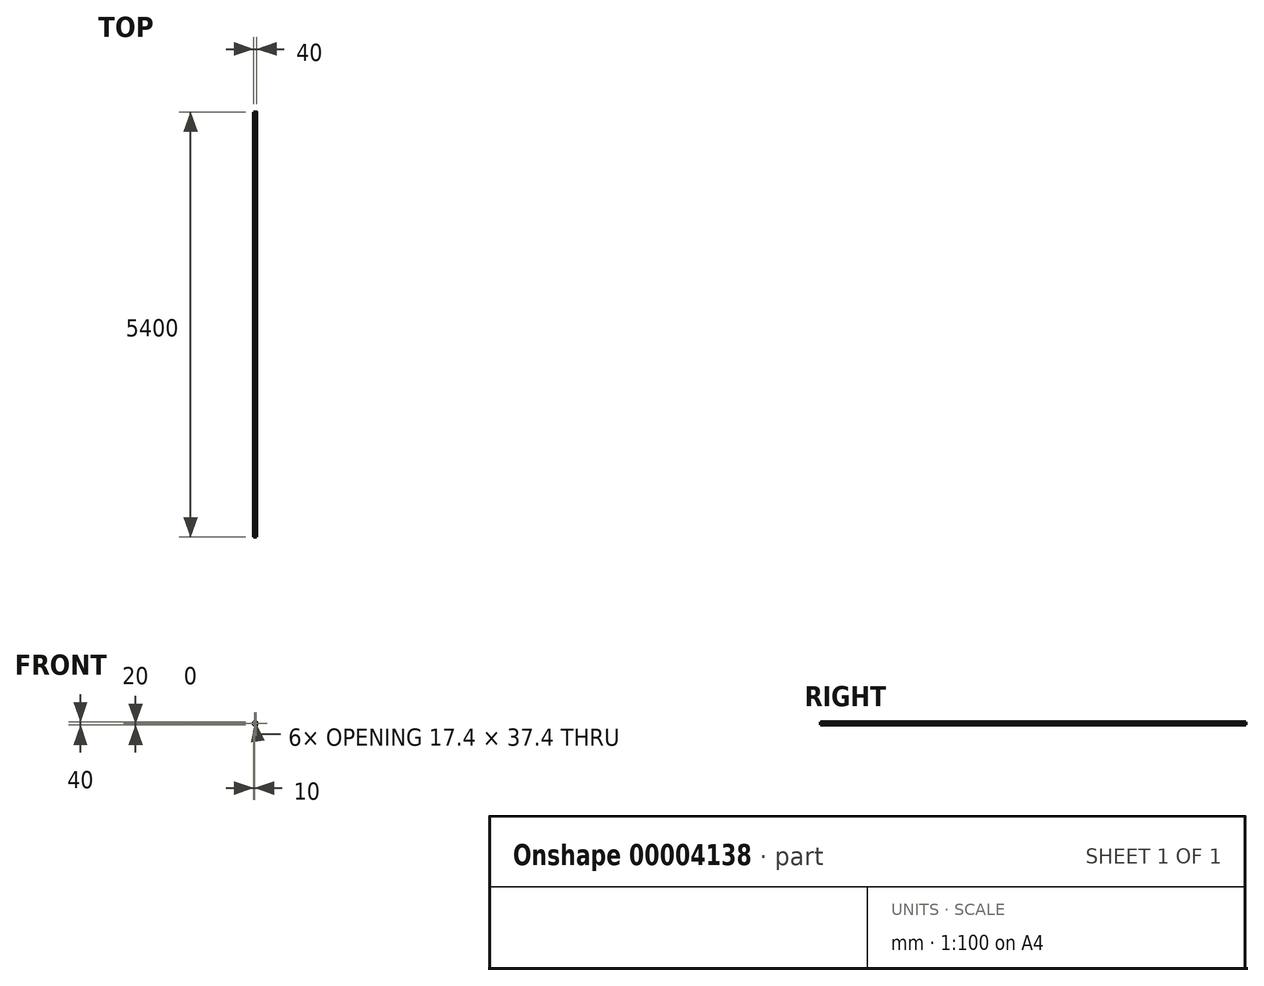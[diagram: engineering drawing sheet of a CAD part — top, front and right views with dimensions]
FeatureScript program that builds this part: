
annotation { "Feature Type Name" : "Feature", "Feature Type Description" : "" }
export const myFeature = defineFeature(function(context is Context, id is Id, definition is map)
    precondition{}
    {
        {
            var Q0;
            Q0=qCreatedBy(makeId("Front.planeOp"),FACE);
            var sketch = newSketch(context, id + "F0", { "sketchPlane" : qUnion([Q0])});
            skLineSegment(sketch, "E0.rect.bottom", {"start": v(20, -20) * mm, "end": v(-20, -20) * mm, "construction": true});
            skLineSegment(sketch, "E0.rect.top", {"start": v(20, 20) * mm, "end": v(-20, 20) * mm, "construction": true});
            skLineSegment(sketch, "E0.rect.left", {"start": v(20, -20) * mm, "end": v(20, 20) * mm, "construction": true});
            skLineSegment(sketch, "E0.rect.right", {"start": v(-20, -20) * mm, "end": v(-20, 20) * mm, "construction": true});
            skPoint(sketch, "E0.rect.middle", {"position": v(0, 0) * mm});
            skLineSegment(sketch, "E1", {"start": v(0, 20) * mm, "end": v(0, -20) * mm, "construction": true});
            skLineSegment(sketch, "E2", {"start": v(20, -20) * mm, "end": v(20, -5.5) * mm});
            skLineSegment(sketch, "E3", {"start": v(20, 5.5) * mm, "end": v(20, 20) * mm});
            skLineSegment(sketch, "E4", {"start": v(20, 20) * mm, "end": v(4.2, 20) * mm});
            skLineSegment(sketch, "E5", {"start": v(20, -20) * mm, "end": v(5.2, -20) * mm});
            skArc(sketch, "E6", {"start": v(20, 5.5) * mm, "mid": v(18.29, 0) * mm, "end": v(20, -5.5) * mm});
            skLineSegment(sketch, "E7", {"start": v(5.2, -20) * mm, "end": v(5.2, -17) * mm});
            skLineSegment(sketch, "E8", {"start": v(5.2, -17) * mm, "end": v(8.6, -17) * mm});
            skLineSegment(sketch, "E9", {"start": v(8.6, -17) * mm, "end": v(8.6, -9.1) * mm});
            skLineSegment(sketch, "E10", {"start": v(0, -9.1) * mm, "end": v(0, 2.5) * mm});
            skLineSegment(sketch, "E11", {"start": v(6.7, 17) * mm, "end": v(6.7, 14) * mm});
            skArc(sketch, "E12", {"start": v(6.7, 9) * mm, "mid": v(7.58, 11.5) * mm, "end": v(6.7, 14) * mm});
            skLineSegment(sketch, "E13", {"start": v(4, 6) * mm, "end": v(6.7, 6) * mm});
            skLineSegment(sketch, "E14", {"start": v(6.7, 6) * mm, "end": v(6.7, 9) * mm});
            skLineSegment(sketch, "E15", {"start": v(4, 6) * mm, "end": v(4, 2.5) * mm});
            skLineSegment(sketch, "E16", {"start": v(4, 2.5) * mm, "end": v(0, 2.5) * mm});
            skLineSegment(sketch, "E17", {"start": v(8.6, -9.1) * mm, "end": v(0, -9.1) * mm});
            skLineSegment(sketch, "E18", {"start": v(4.2, 20) * mm, "end": v(4.2, 17) * mm});
            skLineSegment(sketch, "E19", {"start": v(4.2, 17) * mm, "end": v(6.7, 17) * mm});
            skLineSegment(sketch, "E20.0", {"start": v(18.7, 5.9) * mm, "end": v(18.7, 18.7) * mm});
            skArc(sketch, "E20.1", {"start": v(18.7, 5.9) * mm, "mid": v(16.99, 0) * mm, "end": v(18.7, -5.9) * mm});
            skLineSegment(sketch, "E20.2", {"start": v(18.7, -18.7) * mm, "end": v(18.7, -5.9) * mm});
            skLineSegment(sketch, "E20.3", {"start": v(18.7, -18.7) * mm, "end": v(9.9, -18.7) * mm});
            skLineSegment(sketch, "E20.4", {"start": v(9.9, -18.7) * mm, "end": v(9.9, -7.8) * mm});
            skLineSegment(sketch, "E20.5", {"start": v(18.7, 18.7) * mm, "end": v(8, 18.7) * mm});
            skLineSegment(sketch, "E20.6", {"start": v(9.9, -7.8) * mm, "end": v(1.3, -7.8) * mm});
            skLineSegment(sketch, "E20.7", {"start": v(1.3, -7.8) * mm, "end": v(1.3, 1.2) * mm});
            skLineSegment(sketch, "E20.8", {"start": v(5.3, 1.2) * mm, "end": v(1.3, 1.2) * mm});
            skLineSegment(sketch, "E20.9", {"start": v(5.3, 4.7) * mm, "end": v(5.3, 1.2) * mm});
            skLineSegment(sketch, "E20.10", {"start": v(5.3, 4.7) * mm, "end": v(8, 4.7) * mm});
            skLineSegment(sketch, "E20.11", {"start": v(8, 4.7) * mm, "end": v(8, 8.58) * mm});
            skArc(sketch, "E20.12", {"start": v(8, 8.58) * mm, "mid": v(8.88, 11.5) * mm, "end": v(8, 14.42) * mm});
            skLineSegment(sketch, "E20.13", {"start": v(8, 18.7) * mm, "end": v(8, 14.42) * mm});
            skLineSegment(sketch, "E21.0.MirrorCS", {"start": v(-4.2, 20) * mm, "end": v(-4.2, 17) * mm});
            skLineSegment(sketch, "E21.1.MirrorCS", {"start": v(-4.2, 17) * mm, "end": v(-6.7, 17) * mm});
            skLineSegment(sketch, "E21.2.MirrorCS", {"start": v(-6.7, 17) * mm, "end": v(-6.7, 14) * mm});
            skLineSegment(sketch, "E21.3.MirrorCS", {"start": v(-8, 18.7) * mm, "end": v(-8, 14.42) * mm});
            skArc(sketch, "E21.4.MirrorCS", {"start": v(-8, 8.58) * mm, "mid": v(-8.88, 11.5) * mm, "end": v(-8, 14.42) * mm});
            skArc(sketch, "E21.5.MirrorCS", {"start": v(-6.7, 9) * mm, "mid": v(-7.58, 11.5) * mm, "end": v(-6.7, 14) * mm});
            skLineSegment(sketch, "E21.6.MirrorCS", {"start": v(-6.7, 6) * mm, "end": v(-6.7, 9) * mm});
            skLineSegment(sketch, "E21.7.MirrorCS", {"start": v(-8, 4.7) * mm, "end": v(-8, 8.58) * mm});
            skLineSegment(sketch, "E21.8.MirrorCS", {"start": v(-5.3, 4.7) * mm, "end": v(-8, 4.7) * mm});
            skLineSegment(sketch, "E21.9.MirrorCS", {"start": v(-4, 6) * mm, "end": v(-6.7, 6) * mm});
            skLineSegment(sketch, "E21.10.MirrorCS", {"start": v(-4, 6) * mm, "end": v(-4, 2.5) * mm});
            skLineSegment(sketch, "E21.11.MirrorCS", {"start": v(-5.3, 4.7) * mm, "end": v(-5.3, 1.2) * mm});
            skLineSegment(sketch, "E21.12.MirrorCS", {"start": v(-5.3, 1.2) * mm, "end": v(-1.3, 1.2) * mm});
            skLineSegment(sketch, "E21.13.MirrorCS", {"start": v(-4, 2.5) * mm, "end": v(0, 2.5) * mm});
            skLineSegment(sketch, "E21.14.MirrorCS", {"start": v(-1.3, -7.8) * mm, "end": v(-1.3, 1.2) * mm});
            skLineSegment(sketch, "E21.15.MirrorCS", {"start": v(-8.6, -9.1) * mm, "end": v(0, -9.1) * mm});
            skLineSegment(sketch, "E21.16.MirrorCS", {"start": v(-9.9, -7.8) * mm, "end": v(-1.3, -7.8) * mm});
            skLineSegment(sketch, "E21.17.MirrorCS", {"start": v(-9.9, -18.7) * mm, "end": v(-9.9, -7.8) * mm});
            skLineSegment(sketch, "E21.18.MirrorCS", {"start": v(-8.6, -17) * mm, "end": v(-8.6, -9.1) * mm});
            skLineSegment(sketch, "E21.19.MirrorCS", {"start": v(-5.2, -17) * mm, "end": v(-8.6, -17) * mm});
            skLineSegment(sketch, "E21.20.MirrorCS", {"start": v(-5.2, -20) * mm, "end": v(-5.2, -17) * mm});
            skLineSegment(sketch, "E21.21.MirrorCS", {"start": v(-18.7, -18.7) * mm, "end": v(-9.9, -18.7) * mm});
            skLineSegment(sketch, "E21.22.MirrorCS", {"start": v(-20, -20) * mm, "end": v(-5.2, -20) * mm});
            skLineSegment(sketch, "E21.23.MirrorCS", {"start": v(-18.7, -18.7) * mm, "end": v(-18.7, -5.9) * mm});
            skLineSegment(sketch, "E21.24.MirrorCS", {"start": v(-20, -20) * mm, "end": v(-20, -5.5) * mm});
            skArc(sketch, "E21.25.MirrorCS", {"start": v(-18.7, 5.9) * mm, "mid": v(-16.99, 0) * mm, "end": v(-18.7, -5.9) * mm});
            skArc(sketch, "E21.26.MirrorCS", {"start": v(-20, 5.5) * mm, "mid": v(-18.29, 0) * mm, "end": v(-20, -5.5) * mm});
            skLineSegment(sketch, "E21.27.MirrorCS", {"start": v(-18.7, 5.9) * mm, "end": v(-18.7, 18.7) * mm});
            skLineSegment(sketch, "E21.28.MirrorCS", {"start": v(-20, 5.5) * mm, "end": v(-20, 20) * mm});
            skLineSegment(sketch, "E21.29.MirrorCS", {"start": v(-20, 20) * mm, "end": v(-4.2, 20) * mm});
            skLineSegment(sketch, "E21.30.MirrorCS", {"start": v(-18.7, 18.7) * mm, "end": v(-8, 18.7) * mm});
            skSolve(sketch);
        }
        {
            var Q0;
            Q0=makeQuery(id+"F0.imprint","IMPRINT",FACE,{"disambiguationData":[TD([[makeQuery(id+"F0.imprint","IMPRINT",EDGE,{"derivedFrom":sQuery(id+"F0.wireOp",EDGE,"E2")}),1.0]])]});
            var Q1;
            Q1=makeQuery(id+"F0.imprint","IMPRINT",FACE,{"disambiguationData":[TD([[makeQuery(id+"F0.imprint","IMPRINT",EDGE,{"derivedFrom":sQuery(id+"F0.wireOp",EDGE,"E10")}),1.0]])]});
            extrude(context, id + "F1", {"entities" : qUnion([Q0, Q1]), "oppositeDirection" : true, "depth" : 50 * mm});
        }
        {
            var Q0;
            Q0=makeQuery(id+"F0.imprint","IMPRINT",FACE,{"disambiguationData":[TD([[makeQuery(id+"F0.imprint","IMPRINT",EDGE,{"derivedFrom":sQuery(id+"F0.wireOp",EDGE,"E10")}),1.0]])]});
            var Q1;
            Q1=makeQuery(id+"F0.imprint","IMPRINT",FACE,{"disambiguationData":[TD([[makeQuery(id+"F0.imprint","IMPRINT",EDGE,{"derivedFrom":sQuery(id+"F0.wireOp",EDGE,"E2")}),1.0]])]});
            extrude(context, id + "F2", {"entities" : qUnion([Q0, Q1]), "oppositeDirection" : true, "depth" : 3500 * mm});
        }
        {
            var Q0;
            Q0=makeQuery(id+"F0.imprint","IMPRINT",FACE,{"disambiguationData":[TD([[makeQuery(id+"F0.imprint","IMPRINT",EDGE,{"derivedFrom":sQuery(id+"F0.wireOp",EDGE,"E10")}),1.0]])]});
            var Q1;
            Q1=makeQuery(id+"F0.imprint","IMPRINT",FACE,{"disambiguationData":[TD([[makeQuery(id+"F0.imprint","IMPRINT",EDGE,{"derivedFrom":sQuery(id+"F0.wireOp",EDGE,"E2")}),1.0]])]});
            extrude(context, id + "F3", {"entities" : qUnion([Q0, Q1]), "oppositeDirection" : true, "depth" : (3 * 1800) * mm});
        }
        {
            var Q0;
            Q0=makeQuery(id+"F1.opExtrude","SWEPT_EDGE",EDGE,{"disambiguationData":[OSD([sQuery(id+"F0.wireOp",EDGE,"E21.28.MirrorCS"),sQuery(id+"F0.wireOp",EDGE,"E21.29.MirrorCS")])]});
            var Q1;
            Q1=makeQuery(id+"F1.opExtrude","SWEPT_EDGE",EDGE,{"disambiguationData":[OSD([sQuery(id+"F0.wireOp",EDGE,"E21.0.MirrorCS"),sQuery(id+"F0.wireOp",EDGE,"E21.29.MirrorCS")])]});
            var Q2;
            Q2=makeQuery(id+"F1.opExtrude","SWEPT_EDGE",EDGE,{"disambiguationData":[OSD([sQuery(id+"F0.wireOp",EDGE,"E4"),sQuery(id+"F0.wireOp",EDGE,"E18")])]});
            var Q3;
            Q3=makeQuery(id+"F1.opExtrude","SWEPT_EDGE",EDGE,{"disambiguationData":[OSD([sQuery(id+"F0.wireOp",EDGE,"E3"),sQuery(id+"F0.wireOp",EDGE,"E4")])]});
            var Q4;
            Q4=makeQuery(id+"F1.opExtrude","SWEPT_EDGE",EDGE,{"disambiguationData":[OSD([sQuery(id+"F0.wireOp",EDGE,"E21.22.MirrorCS"),sQuery(id+"F0.wireOp",EDGE,"E21.24.MirrorCS")])]});
            var Q5;
            Q5=makeQuery(id+"F1.opExtrude","SWEPT_EDGE",EDGE,{"disambiguationData":[OSD([sQuery(id+"F0.wireOp",EDGE,"E2"),sQuery(id+"F0.wireOp",EDGE,"E5")])]});
            var Q6;
            Q6=makeQuery(id+"F1.opExtrude","SWEPT_EDGE",EDGE,{"disambiguationData":[OSD([sQuery(id+"F0.wireOp",EDGE,"E20.4"),sQuery(id+"F0.wireOp",EDGE,"E20.6")])]});
            var Q7;
            Q7=makeQuery(id+"F1.opExtrude","SWEPT_EDGE",EDGE,{"disambiguationData":[OSD([sQuery(id+"F0.wireOp",EDGE,"E21.16.MirrorCS"),sQuery(id+"F0.wireOp",EDGE,"E21.17.MirrorCS")])]});
            var Q8;
            Q8=makeQuery(id+"F1.opExtrude","SWEPT_EDGE",EDGE,{"disambiguationData":[OSD([sQuery(id+"F0.wireOp",EDGE,"E20.4"),sQuery(id+"F0.wireOp",EDGE,"E20.6")])]});
            var Q9;
            Q9=makeQuery(id+"F1.opExtrude","SWEPT_EDGE",EDGE,{"disambiguationData":[OSD([sQuery(id+"F0.wireOp",EDGE,"E21.16.MirrorCS"),sQuery(id+"F0.wireOp",EDGE,"E21.17.MirrorCS")])]});
            fillet(context, id + "F4", {"entities" : qUnion([Q0, Q1, Q2, Q3, Q4, Q5, Q6, Q7, Q8, Q9]), "radius" : 0.8 * mm, "tangentPropagation" : true, "allowEdgeOverflow" : false});
        }
        {
            var Q0;
            Q0=makeQuery(id+"F1.opExtrude","SWEPT_EDGE",EDGE,{"disambiguationData":[OSD([sQuery(id+"F0.wireOp",EDGE,"E15"),sQuery(id+"F0.wireOp",EDGE,"E16")])]});
            var Q1;
            Q1=makeQuery(id+"F1.opExtrude","SWEPT_EDGE",EDGE,{"disambiguationData":[OSD([sQuery(id+"F0.wireOp",EDGE,"E13"),sQuery(id+"F0.wireOp",EDGE,"E15")])]});
            var Q2;
            Q2=makeQuery(id+"F1.opExtrude","SWEPT_EDGE",EDGE,{"disambiguationData":[OSD([sQuery(id+"F0.wireOp",EDGE,"E13"),sQuery(id+"F0.wireOp",EDGE,"E14")])]});
            var Q3;
            Q3=makeQuery(id+"F1.opExtrude","SWEPT_EDGE",EDGE,{"disambiguationData":[OSD([sQuery(id+"F0.wireOp",EDGE,"E12"),sQuery(id+"F0.wireOp",EDGE,"E14")])]});
            var Q4;
            Q4=makeQuery(id+"F1.opExtrude","SWEPT_EDGE",EDGE,{"disambiguationData":[OSD([sQuery(id+"F0.wireOp",EDGE,"E11"),sQuery(id+"F0.wireOp",EDGE,"E12")])]});
            var Q5;
            Q5=makeQuery(id+"F1.opExtrude","SWEPT_EDGE",EDGE,{"disambiguationData":[OSD([sQuery(id+"F0.wireOp",EDGE,"E21.2.MirrorCS"),sQuery(id+"F0.wireOp",EDGE,"E21.5.MirrorCS")])]});
            var Q6;
            Q6=makeQuery(id+"F1.opExtrude","SWEPT_EDGE",EDGE,{"disambiguationData":[OSD([sQuery(id+"F0.wireOp",EDGE,"E21.5.MirrorCS"),sQuery(id+"F0.wireOp",EDGE,"E21.6.MirrorCS")])]});
            var Q7;
            Q7=makeQuery(id+"F1.opExtrude","SWEPT_EDGE",EDGE,{"disambiguationData":[OSD([sQuery(id+"F0.wireOp",EDGE,"E21.9.MirrorCS"),sQuery(id+"F0.wireOp",EDGE,"E21.10.MirrorCS")])]});
            var Q8;
            Q8=makeQuery(id+"F1.opExtrude","SWEPT_EDGE",EDGE,{"disambiguationData":[OSD([sQuery(id+"F0.wireOp",EDGE,"E21.10.MirrorCS"),sQuery(id+"F0.wireOp",EDGE,"E21.13.MirrorCS")])]});
            fillet(context, id + "F5", {"entities" : qUnion([Q0, Q1, Q2, Q3, Q4, Q5, Q6, Q7, Q8]), "radius" : 0.8 * mm, "tangentPropagation" : true, "allowEdgeOverflow" : false});
        }
        {
            var Q0;
            Q0=makeQuery(id+"F1.opExtrude","SWEPT_EDGE",EDGE,{"disambiguationData":[OSD([sQuery(id+"F0.wireOp",EDGE,"E20.6"),sQuery(id+"F0.wireOp",EDGE,"E20.7")])]});
            var Q1;
            Q1=makeQuery(id+"F1.opExtrude","SWEPT_EDGE",EDGE,{"disambiguationData":[OSD([sQuery(id+"F0.wireOp",EDGE,"E20.7"),sQuery(id+"F0.wireOp",EDGE,"E20.8")])]});
            var Q2;
            Q2=makeQuery(id+"F1.opExtrude","SWEPT_EDGE",EDGE,{"disambiguationData":[OSD([sQuery(id+"F0.wireOp",EDGE,"E20.8"),sQuery(id+"F0.wireOp",EDGE,"E20.9")])]});
            var Q3;
            Q3=makeQuery(id+"F1.opExtrude","SWEPT_EDGE",EDGE,{"disambiguationData":[OSD([sQuery(id+"F0.wireOp",EDGE,"E20.9"),sQuery(id+"F0.wireOp",EDGE,"E20.10")])]});
            var Q4;
            Q4=makeQuery(id+"F1.opExtrude","SWEPT_EDGE",EDGE,{"disambiguationData":[OSD([sQuery(id+"F0.wireOp",EDGE,"E20.10"),sQuery(id+"F0.wireOp",EDGE,"E20.11")])]});
            var Q5;
            Q5=makeQuery(id+"F1.opExtrude","SWEPT_EDGE",EDGE,{"disambiguationData":[OSD([sQuery(id+"F0.wireOp",EDGE,"E21.14.MirrorCS"),sQuery(id+"F0.wireOp",EDGE,"E21.16.MirrorCS")])]});
            var Q6;
            Q6=makeQuery(id+"F1.opExtrude","SWEPT_EDGE",EDGE,{"disambiguationData":[OSD([sQuery(id+"F0.wireOp",EDGE,"E21.12.MirrorCS"),sQuery(id+"F0.wireOp",EDGE,"E21.14.MirrorCS")])]});
            var Q7;
            Q7=makeQuery(id+"F1.opExtrude","SWEPT_EDGE",EDGE,{"disambiguationData":[OSD([sQuery(id+"F0.wireOp",EDGE,"E21.11.MirrorCS"),sQuery(id+"F0.wireOp",EDGE,"E21.12.MirrorCS")])]});
            var Q8;
            Q8=makeQuery(id+"F1.opExtrude","SWEPT_EDGE",EDGE,{"disambiguationData":[OSD([sQuery(id+"F0.wireOp",EDGE,"E21.8.MirrorCS"),sQuery(id+"F0.wireOp",EDGE,"E21.11.MirrorCS")])]});
            var Q9;
            Q9=makeQuery(id+"F1.opExtrude","SWEPT_EDGE",EDGE,{"disambiguationData":[OSD([sQuery(id+"F0.wireOp",EDGE,"E21.7.MirrorCS"),sQuery(id+"F0.wireOp",EDGE,"E21.8.MirrorCS")])]});
            fillet(context, id + "F6", {"entities" : qUnion([Q0, Q1, Q2, Q3, Q4, Q5, Q6, Q7, Q8, Q9]), "radius" : .4 * mm, "tangentPropagation" : true, "allowEdgeOverflow" : false});
        }
        {
            var Q0;
            Q0=makeQuery(id+"F3.opExtrude","SWEPT_EDGE",EDGE,{"disambiguationData":[OSD([sQuery(id+"F0.wireOp",EDGE,"E21.28.MirrorCS"),sQuery(id+"F0.wireOp",EDGE,"E21.29.MirrorCS")])]});
            var Q1;
            Q1=makeQuery(id+"F3.opExtrude","SWEPT_EDGE",EDGE,{"disambiguationData":[OSD([sQuery(id+"F0.wireOp",EDGE,"E3"),sQuery(id+"F0.wireOp",EDGE,"E4")])]});
            var Q2;
            Q2=makeQuery(id+"F3.opExtrude","SWEPT_EDGE",EDGE,{"disambiguationData":[OSD([sQuery(id+"F0.wireOp",EDGE,"E2"),sQuery(id+"F0.wireOp",EDGE,"E5")])]});
            var Q3;
            Q3=makeQuery(id+"F3.opExtrude","SWEPT_EDGE",EDGE,{"disambiguationData":[OSD([sQuery(id+"F0.wireOp",EDGE,"E20.4"),sQuery(id+"F0.wireOp",EDGE,"E20.6")])]});
            var Q4;
            Q4=makeQuery(id+"F3.opExtrude","SWEPT_EDGE",EDGE,{"disambiguationData":[OSD([sQuery(id+"F0.wireOp",EDGE,"E21.16.MirrorCS"),sQuery(id+"F0.wireOp",EDGE,"E21.17.MirrorCS")])]});
            var Q5;
            Q5=makeQuery(id+"F3.opExtrude","SWEPT_EDGE",EDGE,{"disambiguationData":[OSD([sQuery(id+"F0.wireOp",EDGE,"E21.22.MirrorCS"),sQuery(id+"F0.wireOp",EDGE,"E21.24.MirrorCS")])]});
            fillet(context, id + "F7", {"entities" : qUnion([Q0, Q1, Q2, Q3, Q4, Q5]), "radius" : 0.8 * mm, "tangentPropagation" : true, "allowEdgeOverflow" : false});
        }
        {
            var Q0;
            Q0=makeQuery(id+"F3.opExtrude","SWEPT_EDGE",EDGE,{"disambiguationData":[OSD([sQuery(id+"F0.wireOp",EDGE,"E21.2.MirrorCS"),sQuery(id+"F0.wireOp",EDGE,"E21.5.MirrorCS")])]});
            var Q1;
            Q1=makeQuery(id+"F3.opExtrude","SWEPT_EDGE",EDGE,{"disambiguationData":[OSD([sQuery(id+"F0.wireOp",EDGE,"E21.5.MirrorCS"),sQuery(id+"F0.wireOp",EDGE,"E21.6.MirrorCS")])]});
            var Q2;
            Q2=makeQuery(id+"F3.opExtrude","SWEPT_EDGE",EDGE,{"disambiguationData":[OSD([sQuery(id+"F0.wireOp",EDGE,"E21.6.MirrorCS"),sQuery(id+"F0.wireOp",EDGE,"E21.9.MirrorCS")])]});
            var Q3;
            Q3=makeQuery(id+"F3.opExtrude","SWEPT_EDGE",EDGE,{"disambiguationData":[OSD([sQuery(id+"F0.wireOp",EDGE,"E21.9.MirrorCS"),sQuery(id+"F0.wireOp",EDGE,"E21.10.MirrorCS")])]});
            var Q4;
            Q4=makeQuery(id+"F3.opExtrude","SWEPT_EDGE",EDGE,{"disambiguationData":[OSD([sQuery(id+"F0.wireOp",EDGE,"E21.10.MirrorCS"),sQuery(id+"F0.wireOp",EDGE,"E21.13.MirrorCS")])]});
            var Q5;
            Q5=makeQuery(id+"F3.opExtrude","SWEPT_EDGE",EDGE,{"disambiguationData":[OSD([sQuery(id+"F0.wireOp",EDGE,"E15"),sQuery(id+"F0.wireOp",EDGE,"E16")])]});
            var Q6;
            Q6=makeQuery(id+"F3.opExtrude","SWEPT_EDGE",EDGE,{"disambiguationData":[OSD([sQuery(id+"F0.wireOp",EDGE,"E13"),sQuery(id+"F0.wireOp",EDGE,"E15")])]});
            var Q7;
            Q7=makeQuery(id+"F3.opExtrude","SWEPT_EDGE",EDGE,{"disambiguationData":[OSD([sQuery(id+"F0.wireOp",EDGE,"E13"),sQuery(id+"F0.wireOp",EDGE,"E14")])]});
            var Q8;
            Q8=makeQuery(id+"F3.opExtrude","SWEPT_EDGE",EDGE,{"disambiguationData":[OSD([sQuery(id+"F0.wireOp",EDGE,"E12"),sQuery(id+"F0.wireOp",EDGE,"E14")])]});
            var Q9;
            Q9=makeQuery(id+"F3.opExtrude","SWEPT_EDGE",EDGE,{"disambiguationData":[OSD([sQuery(id+"F0.wireOp",EDGE,"E11"),sQuery(id+"F0.wireOp",EDGE,"E12")])]});
            fillet(context, id + "F8", {"entities" : qUnion([Q0, Q1, Q2, Q3, Q4, Q5, Q6, Q7, Q8, Q9]), "radius" : 0.6 * mm, "tangentPropagation" : true, "allowEdgeOverflow" : false});
        }
        {
            var Q0;
            Q0=makeQuery(id+"F3.opExtrude","SWEPT_EDGE",EDGE,{"disambiguationData":[OSD([sQuery(id+"F0.wireOp",EDGE,"E20.10"),sQuery(id+"F0.wireOp",EDGE,"E20.11")])]});
            var Q1;
            Q1=makeQuery(id+"F3.opExtrude","SWEPT_EDGE",EDGE,{"disambiguationData":[OSD([sQuery(id+"F0.wireOp",EDGE,"E20.8"),sQuery(id+"F0.wireOp",EDGE,"E20.9")])]});
            var Q2;
            Q2=makeQuery(id+"F3.opExtrude","SWEPT_EDGE",EDGE,{"disambiguationData":[OSD([sQuery(id+"F0.wireOp",EDGE,"E20.9"),sQuery(id+"F0.wireOp",EDGE,"E20.10")])]});
            var Q3;
            Q3=makeQuery(id+"F3.opExtrude","SWEPT_EDGE",EDGE,{"disambiguationData":[OSD([sQuery(id+"F0.wireOp",EDGE,"E20.7"),sQuery(id+"F0.wireOp",EDGE,"E20.8")])]});
            var Q4;
            Q4=makeQuery(id+"F3.opExtrude","SWEPT_EDGE",EDGE,{"disambiguationData":[OSD([sQuery(id+"F0.wireOp",EDGE,"E20.6"),sQuery(id+"F0.wireOp",EDGE,"E20.7")])]});
            var Q5;
            Q5=makeQuery(id+"F3.opExtrude","SWEPT_EDGE",EDGE,{"disambiguationData":[OSD([sQuery(id+"F0.wireOp",EDGE,"E21.14.MirrorCS"),sQuery(id+"F0.wireOp",EDGE,"E21.16.MirrorCS")])]});
            var Q6;
            Q6=makeQuery(id+"F3.opExtrude","SWEPT_EDGE",EDGE,{"disambiguationData":[OSD([sQuery(id+"F0.wireOp",EDGE,"E21.11.MirrorCS"),sQuery(id+"F0.wireOp",EDGE,"E21.12.MirrorCS")])]});
            var Q7;
            Q7=makeQuery(id+"F3.opExtrude","SWEPT_EDGE",EDGE,{"disambiguationData":[OSD([sQuery(id+"F0.wireOp",EDGE,"E21.8.MirrorCS"),sQuery(id+"F0.wireOp",EDGE,"E21.11.MirrorCS")])]});
            var Q8;
            Q8=makeQuery(id+"F3.opExtrude","SWEPT_EDGE",EDGE,{"disambiguationData":[OSD([sQuery(id+"F0.wireOp",EDGE,"E21.7.MirrorCS"),sQuery(id+"F0.wireOp",EDGE,"E21.8.MirrorCS")])]});
            fillet(context, id + "F9", {"entities" : qUnion([Q0, Q1, Q2, Q3, Q4, Q5, Q6, Q7, Q8]), "radius" : 0.4 * mm, "tangentPropagation" : true, "allowEdgeOverflow" : false});
        }
        {
            var Q0;
            Q0=makeQuery(id+"F2.opExtrude","SWEPT_EDGE",EDGE,{"disambiguationData":[OSD([sQuery(id+"F0.wireOp",EDGE,"E21.28.MirrorCS"),sQuery(id+"F0.wireOp",EDGE,"E21.29.MirrorCS")])]});
            var Q1;
            Q1=makeQuery(id+"F2.opExtrude","SWEPT_EDGE",EDGE,{"disambiguationData":[OSD([sQuery(id+"F0.wireOp",EDGE,"E21.0.MirrorCS"),sQuery(id+"F0.wireOp",EDGE,"E21.29.MirrorCS")])]});
            var Q2;
            Q2=makeQuery(id+"F2.opExtrude","SWEPT_EDGE",EDGE,{"disambiguationData":[OSD([sQuery(id+"F0.wireOp",EDGE,"E3"),sQuery(id+"F0.wireOp",EDGE,"E4")])]});
            var Q3;
            Q3=makeQuery(id+"F2.opExtrude","SWEPT_EDGE",EDGE,{"disambiguationData":[OSD([sQuery(id+"F0.wireOp",EDGE,"E4"),sQuery(id+"F0.wireOp",EDGE,"E18")])]});
            var Q4;
            Q4=makeQuery(id+"F2.opExtrude","SWEPT_EDGE",EDGE,{"disambiguationData":[OSD([sQuery(id+"F0.wireOp",EDGE,"E21.22.MirrorCS"),sQuery(id+"F0.wireOp",EDGE,"E21.24.MirrorCS")])]});
            var Q5;
            Q5=makeQuery(id+"F2.opExtrude","SWEPT_EDGE",EDGE,{"disambiguationData":[OSD([sQuery(id+"F0.wireOp",EDGE,"E2"),sQuery(id+"F0.wireOp",EDGE,"E5")])]});
            var Q6;
            Q6=makeQuery(id+"F2.opExtrude","SWEPT_EDGE",EDGE,{"disambiguationData":[OSD([sQuery(id+"F0.wireOp",EDGE,"E21.15.MirrorCS"),sQuery(id+"F0.wireOp",EDGE,"E21.18.MirrorCS")])]});
            var Q7;
            Q7=makeQuery(id+"F2.opExtrude","SWEPT_EDGE",EDGE,{"disambiguationData":[OSD([sQuery(id+"F0.wireOp",EDGE,"E9"),sQuery(id+"F0.wireOp",EDGE,"E17")])]});
            fillet(context, id + "F10", {"entities" : qUnion([Q0, Q1, Q2, Q3, Q4, Q5, Q6, Q7]), "radius" : 0.8 * mm, "tangentPropagation" : true, "allowEdgeOverflow" : false});
        }
    });
